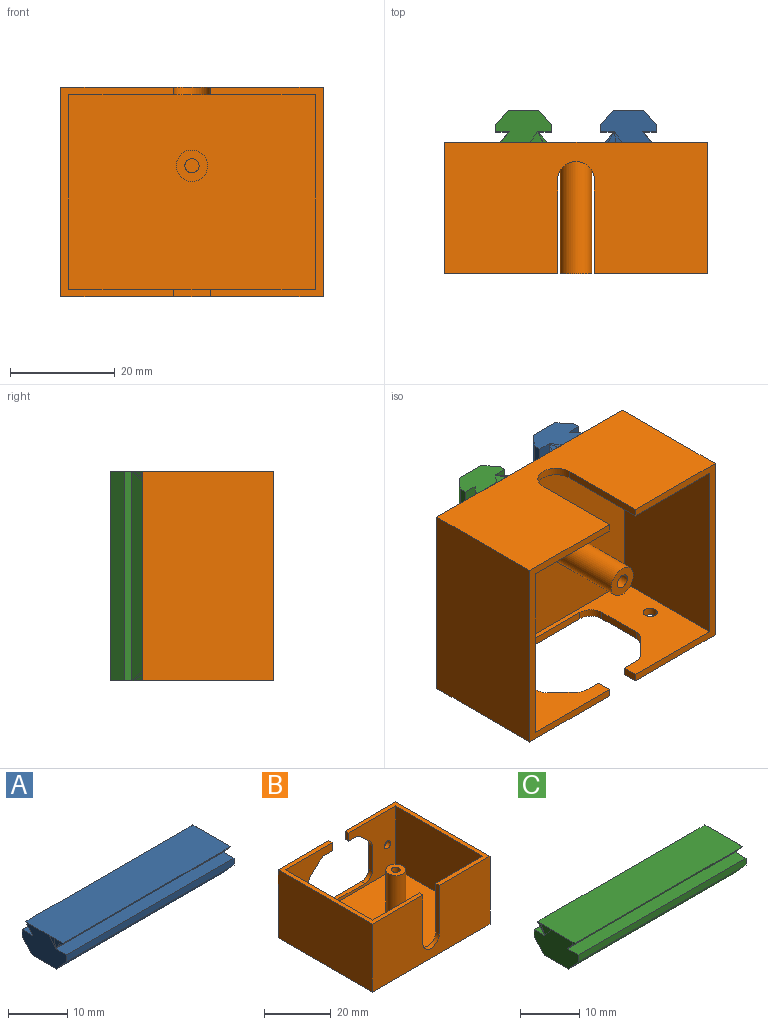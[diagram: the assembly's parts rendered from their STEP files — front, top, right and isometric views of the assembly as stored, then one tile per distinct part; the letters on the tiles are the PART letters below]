
ASSEMBLY  parts=3 mates=2
PART A: 54 faces, bbox 40x10.6x6.1 mm
  f0: plane 10.6x4.1mm, normal (1,0,0), area 37mm2, adj f1,f2,f3,f4,f5,f6,f7,f8
  f1: plane 6.99x1.78mm, normal (1,0,0), area 4.8mm2, adj f0,f23,f25
  f2: plane 40x1.41mm, normal (0,-1,0), area 56.5mm2, adj f0,f3,f8,f37
  f3: plane 40x2.69mm, normal (0,-0.75,-0.67), area 144.1mm2, adj f0,f2,f4,f37
  f4: plane 40x5.8mm, normal (0,0,-1), area 232mm2, adj f0,f3,f5,f37
  f5: plane 40x2.69mm, normal (0,0.75,-0.67), area 144.1mm2, adj f0,f4,f6,f37
  f6: plane 40x1.41mm, normal (0,1,0), area 56.5mm2, adj f0,f5,f7,f37
  f7: plane 40x2.6mm, normal (0,0,1), area 104mm2, adj f0,f6,f10,f37
  f8: plane 40x2.6mm, normal (0,0,1), area 104mm2, adj f0,f2,f31,f37
  f9: plane 0.54x0.49mm, normal (0,0.75,-0.67), area 0.1mm2, adj f49,f50,f53
  f10: plane 40x2mm, normal (0,0.75,-0.67), area 101.8mm2, adj f7,f24,f46,f53
  f11: plane 0.33x0.22mm, normal (0,0.75,-0.67), area 0mm2, adj f12,f22,f53
  f12: plane 0.22x0.19mm, normal (0,0.75,-0.67), area 0mm2, adj f11,f13,f53
  f13: plane 0.22x0.19mm, normal (0.99,0.13,0.01), area 0mm2, adj f12,f14,f53
  f14: plane 0.22x0.05mm, normal (0.98,0.18,-0.01), area 0mm2, adj f13,f15,f53
  f15: plane 0.22x0.02mm, normal (0.99,0.13,0), area 0mm2, adj f14,f21,f53
  f16: plane 0.44x0.22mm, normal (1,0,0), area 0mm2, adj f20,f21,f53
  f17: plane 1.12x0.22mm, normal (1,0,0), area 0mm2, adj f18,f25,f53
  f18: plane 0.75x0.22mm, normal (1,0,0), area 0mm2, adj f17,f19,f53
  f19: plane 0.73x0.22mm, normal (1,0,0), area 0mm2, adj f18,f20,f53
  f20: plane 0.56x0.22mm, normal (1,0,0), area 0mm2, adj f16,f19,f53
  f21: plane 0.22x0.01mm, normal (0.99,0.13,0), area 0mm2, adj f15,f16,f53
  f22: plane 0.74x0.22mm, normal (0,0.75,-0.67), area 0.1mm2, adj f11,f23,f53
  f23: plane 2x1.79mm, normal (0,0.75,-0.67), area 1.5mm2, adj f1,f22,f24,f53
  f24: plane 2.03x2mm, normal (0,0.75,-0.67), area 1.1mm2, adj f10,f23,f53
  f25: plane 8.78x2mm, normal (1,0,0), area 9.4mm2, adj f1,f17,f26,f53
  f26: plane 2x1.79mm, normal (0,-0.75,-0.67), area 0.1mm2, adj f25,f27,f53
  f27: plane 2x1.79mm, normal (0,-0.75,-0.67), area 0.1mm2, adj f26,f28,f53
  f28: plane 2x1.79mm, normal (0,-0.75,-0.67), area 0.1mm2, adj f27,f29,f53
  f29: plane 2x1.79mm, normal (0,-0.75,-0.67), area 0.2mm2, adj f28,f30,f53
  f30: plane 2x1.79mm, normal (0,-0.75,-0.67), area 0.7mm2, adj f29,f45,f53
  f31: plane 40x2mm, normal (0,-0.75,-0.67), area 101.9mm2, adj f8,f32,f43,f53
  f32: plane 2x2mm, normal (0,-0.75,-0.67), area 0.6mm2, adj f31,f42,f53
  f33: plane 2x1.79mm, normal (0,-0.75,-0.67), area 0.4mm2, adj f34,f39,f53
  f34: plane 2x1.79mm, normal (0,-0.75,-0.67), area 0.3mm2, adj f33,f35,f53
  f35: plane 2x1.79mm, normal (-1,-0.01,0.01), area 0.6mm2, adj f34,f36,f53
  f36: plane 2x1.49mm, normal (-1,-0.01,0.01), area 1.5mm2, adj f35,f38,f53
  f37: plane 10.6x6.1mm, normal (-1,0,0), area 48mm2, adj f2,f3,f4,f5,f6,f7,f8,f38
  f38: plane 2x1.49mm, normal (-1,-0.01,0.01), area 1.2mm2, adj f36,f37,f53
  f39: plane 2x1.79mm, normal (0,-0.75,-0.67), area 0.1mm2, adj f33,f40,f53
  f40: plane 2x1.79mm, normal (0,-0.75,-0.67), area 0.5mm2, adj f39,f41,f53
  f41: plane 2x1.79mm, normal (0,-0.75,-0.67), area 0.4mm2, adj f40,f42,f53
  f42: plane 2x1.79mm, normal (0,-0.75,-0.66), area 0.4mm2, adj f32,f41,f53
  f43: plane 2x2mm, normal (0,-0.75,-0.67), area 0.5mm2, adj f31,f44,f53
  f44: plane 2x1.79mm, normal (0,-0.75,-0.67), area 0.8mm2, adj f43,f45,f53
  f45: plane 2x1.79mm, normal (0,-0.75,-0.67), area 0.1mm2, adj f30,f44,f53
  f46: plane 2.03x2mm, normal (0,0.75,-0.67), area 1mm2, adj f10,f47,f53
  f47: plane 2x1.79mm, normal (0,0.75,-0.67), area 1.3mm2, adj f37,f46,f48,f53
  f48: plane 1.07x0.54mm, normal (0,0.75,-0.67), area 0.2mm2, adj f47,f49,f53
  f49: plane 0.62x0.54mm, normal (0,0.75,-0.67), area 0.1mm2, adj f9,f48,f53
  f50: plane 0.54x0.49mm, normal (-0.99,0.12,-0.01), area 0.1mm2, adj f9,f51,f53
  f51: plane 0.54x0.04mm, normal (-0.99,0.12,-0.01), area 0mm2, adj f50,f52,f53
  f52: plane 0.54x0.04mm, normal (-1,0.05,0), area 0mm2, adj f37,f51,f53
  f53: plane 39.99x8.97mm, normal (0,0,1), area 358.7mm2, adj f9,f10,f11,f12,f13,f14,f15,f16
PART B: 36 faces, bbox 50x40x25 mm
  f0: plane 50x25mm, normal (0,1,0), area 740.8mm2, adj f1,f2,f4,f5,f6,f7,f14,f15
  f1: plane 40x21.5mm, normal (0,0,1), area 120mm2, adj f0,f3,f7,f8,f10,f12,f29,f31
  f2: plane 3.05x1.5mm, normal (0,0,-1), area 4.6mm2, adj f0,f3,f19,f28
  f3: plane 47x23mm, normal (0,-1,0), area 571.8mm2, adj f1,f2,f4,f11,f12,f13,f14,f15
  f4: plane 40x21.5mm, normal (0,0,1), area 120mm2, adj f0,f3,f5,f8,f10,f11,f28,f30
  f5: plane 40x25mm, normal (-1,0,0), area 1000mm2, adj f0,f4,f6,f8
  f6: plane 50x40mm, normal (0,0,-1), area 2000mm2, adj f0,f5,f7,f8
  f7: plane 40x25mm, normal (1,0,0), area 1000mm2, adj f0,f1,f6,f8
  f8: plane 50x25mm, normal (0,-1,0), area 1106.1mm2, adj f1,f4,f5,f6,f7,f9,f30,f31
  f9: cylinder r=3.5mm len=7mm, axis (0,-1,0), area 16.5mm2, adj f8,f10,f30,f31
  f10: plane 47x23mm, normal (0,1,0), area 937.1mm2, adj f1,f4,f9,f11,f12,f13,f30,f31
  f11: plane 37x23mm, normal (1,0,0), area 851mm2, adj f3,f4,f10,f13
  f12: plane 37x23mm, normal (-1,0,0), area 851mm2, adj f1,f3,f10,f13
  f13: plane 47x37mm, normal (0,0,1), area 1710.7mm2, adj f3,f10,f11,f12,f32
  f14: plane 21x1.5mm, normal (0,0,1), area 31.5mm2, adj f0,f3,f15,f25
  f15: cylinder r=3mm len=3mm, axis (0,1,0), area 7.1mm2, adj f0,f3,f14,f16
  f16: plane 9.22x1.5mm, normal (1,0,0), area 13.8mm2, adj f0,f3,f15,f17
  f17: cylinder r=3mm len=2.17mm, axis (0,1,0), area 3.6mm2, adj f0,f3,f16,f18
  f18: plane 3.95x3.78mm, normal (0.69,0,-0.72), area 8.2mm2, adj f0,f3,f17,f19
  f19: cylinder r=3mm len=2.07mm, axis (0,1,0), area 3.4mm2, adj f0,f2,f3,f18
  f20: plane 3.05x1.5mm, normal (0,0,-1), area 4.6mm2, adj f0,f3,f21,f29
  f21: cylinder r=3mm len=2.07mm, axis (0,1,0), area 3.4mm2, adj f0,f3,f20,f22
  f22: plane 3.95x3.78mm, normal (-0.69,0,-0.72), area 8.2mm2, adj f0,f3,f21,f23
  f23: cylinder r=3mm len=2.17mm, axis (0,1,0), area 3.6mm2, adj f0,f3,f22,f24
  f24: plane 9.22x1.5mm, normal (-1,0,0), area 13.8mm2, adj f0,f3,f23,f25
  f25: cylinder r=3mm len=3mm, axis (0,1,0), area 7.1mm2, adj f0,f3,f14,f24
  f26: cylinder r=1.35mm len=2.7mm, axis (0,1,0), area 12.7mm2, adj f0,f3
  f27: cylinder r=1.35mm len=2.7mm, axis (0,1,0), area 12.7mm2, adj f0,f3
  f28: plane 3x1.5mm, normal (1,0,0), area 4.5mm2, adj f0,f2,f3,f4
  f29: plane 3x1.5mm, normal (-1,0,0), area 4.5mm2, adj f0,f1,f3,f20
  f30: plane 17.81x1.5mm, normal (1,0,0), area 26.7mm2, adj f4,f8,f9,f10
  f31: plane 17.81x1.5mm, normal (-1,0,0), area 26.7mm2, adj f1,f8,f9,f10
  f32: cylinder r=3mm len=23mm, axis (0,0,-1), area 433.5mm2, adj f13,f33
  f33: plane 6x6mm, normal (0,0,1), area 22.5mm2, adj f32,f34
  f34: cylinder r=1.35mm len=23mm, axis (0,0,1), area 195.1mm2, adj f33,f35
  f35: plane 2.7x2.7mm, normal (0,0,1), area 5.7mm2, adj f34
PART C: 48 faces, bbox 40x10.6x6.1 mm
  f0: plane 10.6x4.1mm, normal (1,0,0), area 37mm2, adj f1,f2,f3,f4,f5,f6,f7,f8
  f1: plane 6.99x1.78mm, normal (1,0,0), area 4.8mm2, adj f0,f40,f41
  f2: plane 40x1.41mm, normal (0,-1,0), area 56.5mm2, adj f0,f3,f8,f11
  f3: plane 40x2.69mm, normal (0,-0.75,-0.67), area 144.1mm2, adj f0,f2,f4,f11
  f4: plane 40x5.8mm, normal (0,0,-1), area 232mm2, adj f0,f3,f5,f11
  f5: plane 40x2.7mm, normal (0,0.75,-0.66), area 144.5mm2, adj f0,f4,f6,f11
  f6: plane 40x1.4mm, normal (0,1,0), area 56mm2, adj f0,f5,f7,f11
  f7: plane 40x2.6mm, normal (0,0,1), area 104mm2, adj f0,f6,f11,f17
  f8: plane 40x2.6mm, normal (0,0,1), area 104mm2, adj f0,f2,f11,f42
  f9: plane 1.07x0.54mm, normal (0,-0.75,-0.67), area 0.2mm2, adj f10,f45,f47
  f10: plane 0.62x0.54mm, normal (0,-0.75,-0.67), area 0.2mm2, adj f9,f44,f47
  f11: plane 10.6x6.1mm, normal (-1,0,0), area 48mm2, adj f2,f3,f4,f5,f6,f7,f8,f12
  f12: plane 2.41x2mm, normal (-1,0,0), area 2.4mm2, adj f11,f14,f47
  f13: plane 2x1.03mm, normal (-1,0,0), area 0.1mm2, adj f14,f23,f47
  f14: plane 2x0.92mm, normal (-1,0,0), area 0mm2, adj f12,f13,f47
  f15: plane 2x1.79mm, normal (0,0.75,-0.67), area 0.1mm2, adj f16,f23,f47
  f16: plane 2x1.79mm, normal (0,0.75,-0.67), area 0.2mm2, adj f15,f22,f47
  f17: plane 40x2mm, normal (0,0.75,-0.67), area 101.9mm2, adj f7,f18,f29,f47
  f18: plane 2x2mm, normal (0,0.75,-0.67), area 0.3mm2, adj f17,f19,f47
  f19: plane 2x1.79mm, normal (0,0.75,-0.67), area 0.6mm2, adj f18,f20,f47
  f20: plane 2x1.79mm, normal (0,0.75,-0.67), area 0.6mm2, adj f19,f21,f47
  f21: plane 2x1.79mm, normal (0,0.75,-0.67), area 0.6mm2, adj f20,f22,f47
  f22: plane 2x1.79mm, normal (0,0.75,-0.67), area 0.2mm2, adj f16,f21,f47
  f23: plane 2x1.79mm, normal (-1,0,0), area 0.8mm2, adj f13,f15,f47
  f24: plane 2x1.79mm, normal (0,0.75,-0.67), area 0.5mm2, adj f25,f29,f47
  f25: plane 2x1.79mm, normal (0,0.75,-0.67), area 0.7mm2, adj f24,f28,f47
  f26: plane 2x1.79mm, normal (0,0.75,-0.67), area 0.1mm2, adj f27,f40,f47
  f27: plane 2x1.79mm, normal (0,0.75,-0.67), area 0.2mm2, adj f26,f28,f47
  f28: plane 2x1.79mm, normal (0,0.75,-0.67), area 0.6mm2, adj f25,f27,f47
  f29: plane 2x2mm, normal (0,0.75,-0.67), area 0.6mm2, adj f17,f24,f47
  f30: plane 1.08x0.22mm, normal (1,0,0), area 0mm2, adj f39,f40,f47
  f31: plane 0.22x0.22mm, normal (0,-0.75,-0.67), area 0mm2, adj f32,f33,f47
  f32: plane 0.22x0.19mm, normal (0,-0.75,-0.67), area 0mm2, adj f31,f34,f47
  f33: plane 0.74x0.22mm, normal (0,-0.75,-0.67), area 0.1mm2, adj f31,f41,f47
  f34: plane 0.22x0.19mm, normal (0.99,-0.16,-0.01), area 0mm2, adj f32,f35,f47
  f35: plane 0.22x0.04mm, normal (0.99,-0.16,-0.01), area 0mm2, adj f34,f36,f47
  f36: plane 0.22x0.02mm, normal (0.99,-0.13,0), area 0mm2, adj f35,f37,f47
  f37: plane 0.22x0.01mm, normal (0.99,-0.13,0), area 0mm2, adj f36,f38,f47
  f38: plane 0.44x0.22mm, normal (1,0,0), area 0mm2, adj f37,f39,f47
  f39: plane 0.63x0.22mm, normal (1,0,0), area 0mm2, adj f30,f38,f47
  f40: plane 8.78x2mm, normal (1,0,0), area 9.4mm2, adj f1,f26,f30,f47
  f41: plane 2x1.79mm, normal (0,-0.75,-0.67), area 1.5mm2, adj f1,f33,f43,f47
  f42: plane 40x2mm, normal (0,-0.75,-0.67), area 101.8mm2, adj f8,f43,f46,f47
  f43: plane 2.03x2mm, normal (0,-0.75,-0.67), area 1.1mm2, adj f41,f42,f47
  f44: plane 0.54x0.49mm, normal (-1,-0.05,0), area 0.1mm2, adj f10,f11,f47
  f45: plane 2x1.79mm, normal (0,-0.75,-0.67), area 1.3mm2, adj f9,f11,f46,f47
  f46: plane 2.03x2mm, normal (0,-0.75,-0.67), area 1mm2, adj f42,f45,f47
  f47: plane 40x8.97mm, normal (0,0,1), area 358.8mm2, adj f9,f10,f11,f12,f13,f14,f15,f16
PLACE A rot(axis=(0.58,0.58,-0.58),120deg) t=(27.5,6.1,0)mm
PLACE B rot(axis=(0,-0.71,0.71),180deg) t=(25,0,-20)mm fixed
PLACE C rot(axis=(0.58,0.58,-0.58),120deg) t=(27.5,6.1,0)mm
MATE planar B.f6 <-> C.f47  axis (0,1,0) through (0,0,0)mm
MATE planar A.f53 <-> B.f6  axis (0,-1,0) through (10,0,0)mm
